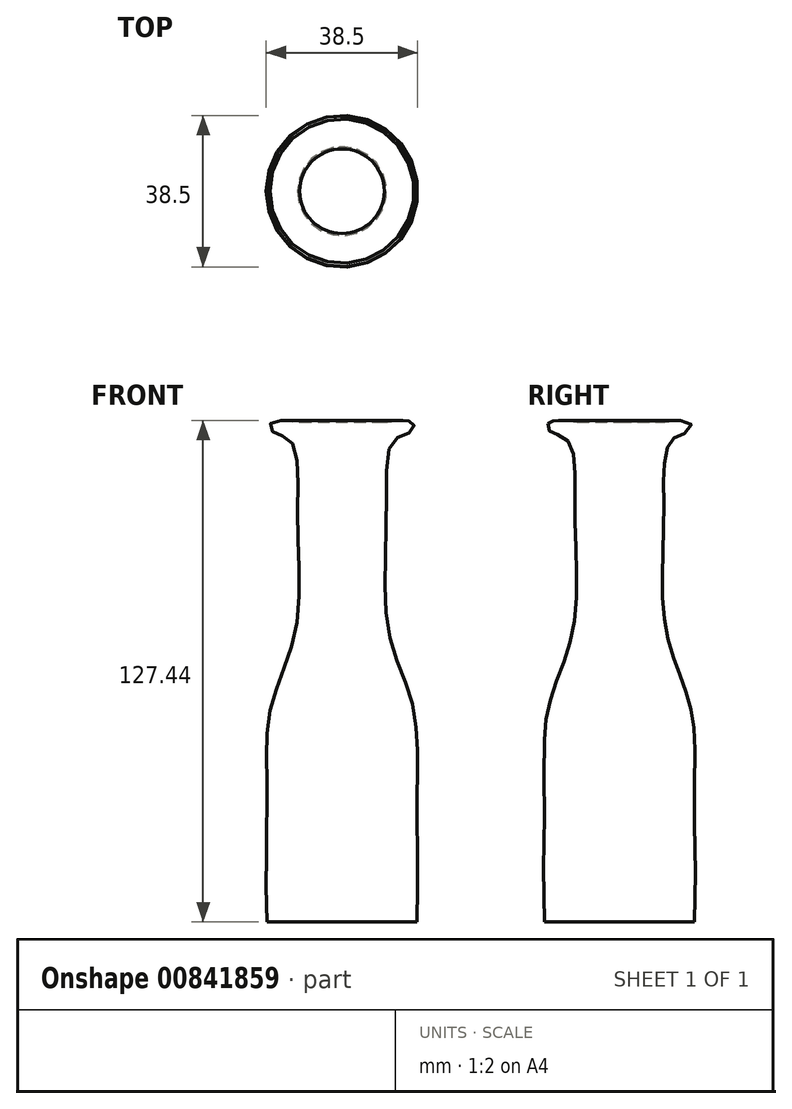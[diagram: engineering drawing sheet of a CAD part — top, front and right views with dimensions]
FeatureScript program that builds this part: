
annotation { "Feature Type Name" : "Feature", "Feature Type Description" : "" }
export const myFeature = defineFeature(function(context is Context, id is Id, definition is map)
    precondition{}
    {
        {
            var Q0;
            Q0=qCreatedBy(makeId("Front.planeOp"),FACE);
            var sketch = newSketch(context, id + "F0", { "sketchPlane" : qUnion([Q0])});
            skLineSegment(sketch, "E0", {"start": v(0, 0) * mm, "end": v(0, 127) * mm});
            skLineSegment(sketch, "E1", {"start": v(0, 0) * mm, "end": v(19.05, 0) * mm});
            skFitSpline(sketch, "E2", {"points": [v(19.05, 0) * mm, v(19.05, 32.44) * mm, v(18.08, 54.45) * mm, v(11.83, 74.01) * mm, v(11.29, 104.17) * mm, v(13.19, 122.37) * mm, v(17.8, 124.82) * mm, v(17.8, 126.99) * mm, v(10.74, 127) * mm], "startDerivative": vector(8.1, 242.28) * mm, "endDerivative": vector(-61.56, -5.86) * mm});
            skLineSegment(sketch, "E3", {"start": v(0, 127) * mm, "end": v(10.74, 127) * mm});
            skSolve(sketch);
        }
        {
            var Q0;
            Q0=makeQuery(id+"F0.imprint","IMPRINT",FACE,{"disambiguationData":[TD([[makeQuery(id+"F0.imprint","IMPRINT",EDGE,{"derivedFrom":sQuery(id+"F0.wireOp",EDGE,"E0")}),-1.0]])]});
            var Q1;
            Q1=sQuery(id+"F0.wireOp",EDGE,"E0");
            revolve(context, id + "F1", {"surfaceOperationType" : NewSurfaceOperationType.NEW, "entities" : qUnion([Q0]), "axis" : qUnion([Q1]), "revolveType" : RevolveType.FULL});
        }
    });
